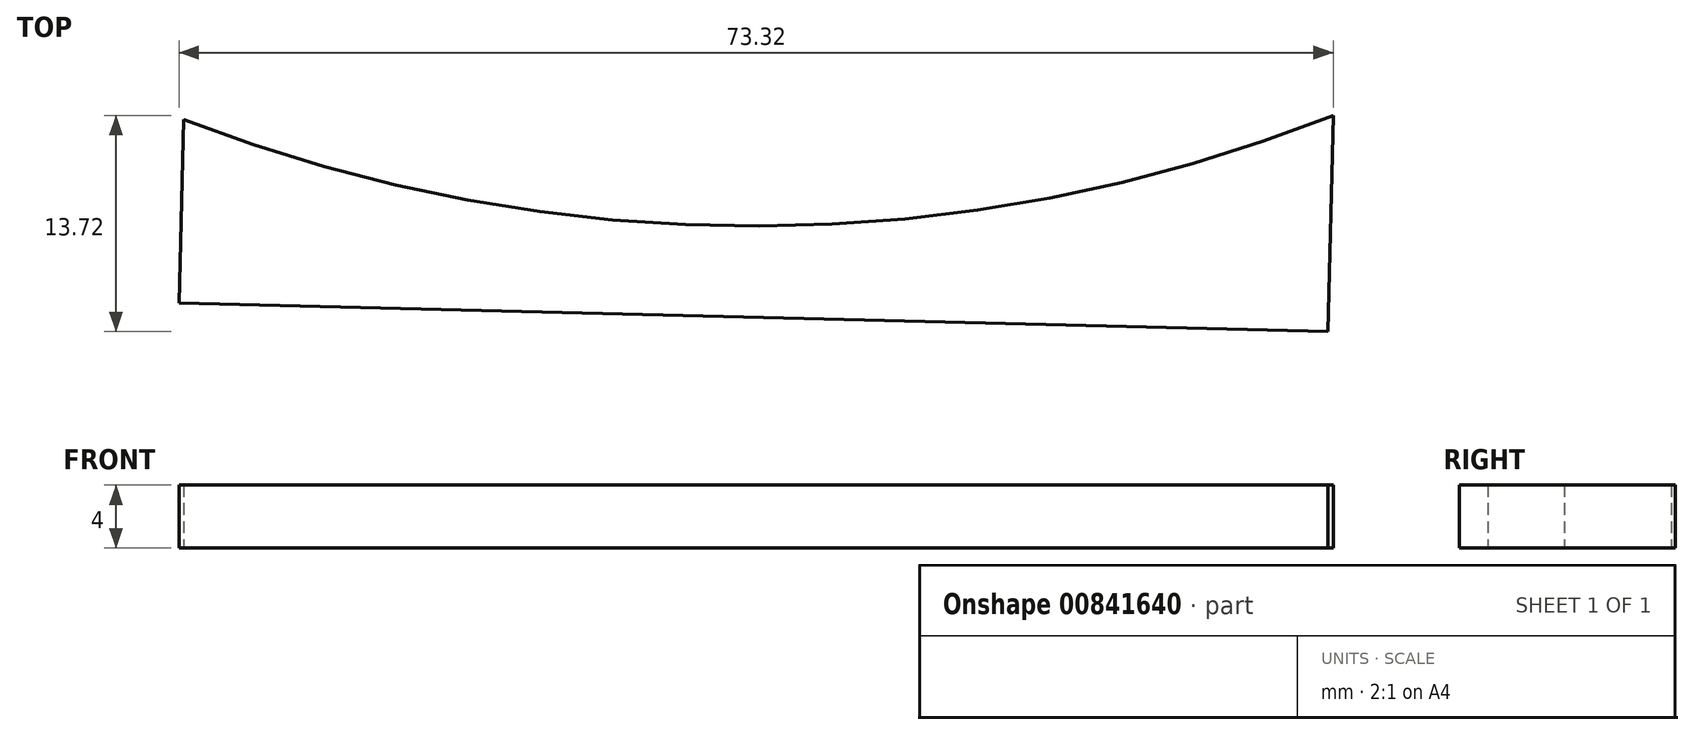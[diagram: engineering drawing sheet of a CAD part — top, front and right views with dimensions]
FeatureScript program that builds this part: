
annotation { "Feature Type Name" : "Feature", "Feature Type Description" : "" }
export const myFeature = defineFeature(function(context is Context, id is Id, definition is map)
    precondition{}
    {
        {
            var Q0;
            Q0=qCreatedBy(makeId("Top.planeOp"),FACE);
            var sketch = newSketch(context, id + "F0", { "sketchPlane" : qUnion([Q0])});
            skArc(sketch, "E0", {"start": v(-36.2, -93.22) * mm, "mid": v(0.34, -100) * mm, "end": v(36.83, -92.97) * mm});
            skPoint(sketch, "E1.middle", {"position": v(0, -100) * mm});
            skLineSegment(sketch, "E2.top", {"start": v(-36.49, -104.86) * mm, "end": v(36.49, -106.69) * mm});
            skLineSegment(sketch, "E2.left", {"start": v(-36.2, -93.22) * mm, "end": v(-36.49, -104.86) * mm});
            skLineSegment(sketch, "E2.right", {"start": v(36.83, -92.97) * mm, "end": v(36.49, -106.69) * mm});
            skLineSegment(sketch, "E3", {"start": v(0, 0) * mm, "end": v(0, -120.71) * mm, "construction": true});
            skPoint(sketch, "E4", {"position": v(0, -105.78) * mm});
            skPoint(sketch, "E4.positionSnap0", {"position": v(0.53, -105.78) * mm});
            skSolve(sketch);
        }
        {
            var Q0;
            Q0=makeQuery(id+"F0.imprint","IMPRINT",FACE,{"disambiguationData":[TD([[makeQuery(id+"F0.imprint","IMPRINT",EDGE,{"derivedFrom":sQuery(id+"F0.wireOp",EDGE,"E0")}),-1.0]])]});
            extrude(context, id + "F1", {"entities" : qUnion([Q0]), "depth" : 4 * mm, "offsetDistance" : 25 * mm});
        }
    });
